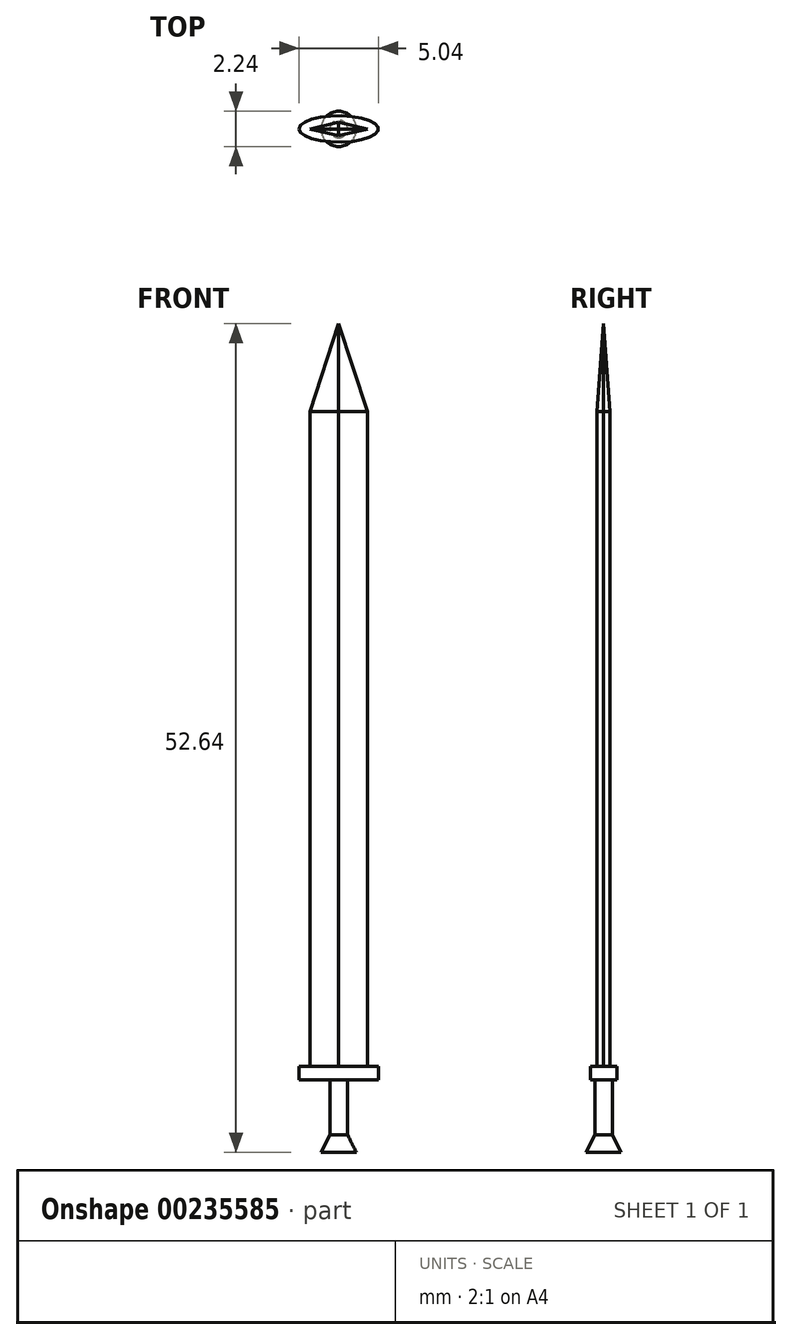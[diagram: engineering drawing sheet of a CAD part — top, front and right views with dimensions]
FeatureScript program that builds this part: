
annotation { "Feature Type Name" : "Feature", "Feature Type Description" : "" }
export const myFeature = defineFeature(function(context is Context, id is Id, definition is map)
    precondition{}
    {
        {
            var Q0;
            Q0=qCreatedBy(makeId("Top.planeOp"),FACE);
            var sketch = newSketch(context, id + "F0", { "sketchPlane" : qUnion([Q0])});
            skCircle(sketch, "E0", {"center": v(12.97, 4.08) * mm, "radius": 0.8 * mm});
            skSolve(sketch);
        }
        {
            var Q0;
            Q0=qCreatedBy(makeId("Top.planeOp"),FACE);
            cPlane(context, id + "F1", {"entities" : qUnion([Q0]), "cplaneType" : CPlaneType.OFFSET, "offset" : 0.8 * mm, "width" : 150 * mm, "height" : 150 * mm});
        }
        {
            var Q0;
            Q0=qCreatedBy(id+"F1.planeOp",FACE);
            var sketch = newSketch(context, id + "F2", { "sketchPlane" : qUnion([Q0])});
            skCircle(sketch, "E1.0", {"center": v(12.97, 4.08) * mm, "radius": 0.8 * mm, "construction": true});
            skCircle(sketch, "E2", {"center": v(12.97, 4.08) * mm, "radius": 0.4 * mm});
            skSolve(sketch);
        }
        {
            var Q0;
            Q0=qCreatedBy(id+"F1.planeOp",FACE);
            cPlane(context, id + "F3", {"entities" : qUnion([Q0]), "cplaneType" : CPlaneType.OFFSET, "offset" : 2.8 * mm, "width" : 150 * mm, "height" : 150 * mm});
        }
        {
            var Q0;
            Q0=qCreatedBy(id+"F3.planeOp",FACE);
            var sketch = newSketch(context, id + "F4", { "sketchPlane" : qUnion([Q0])});
            skCircle(sketch, "E3.0", {"center": v(12.97, 4.08) * mm, "radius": 0.4 * mm, "construction": true});
            skEllipse(sketch, "E4", {"center": v(12.97, 4.08) * mm, "majorRadius": 1.8 * mm, "minorRadius": 0.6 * mm, "majorAxis": v(-1, 0)});
            skSolve(sketch);
        }
        {
            var Q0;
            Q0=makeQuery(id+"F0.imprint","IMPRINT",FACE,{"disambiguationData":[TD([[makeQuery(id+"F0.imprint","IMPRINT",EDGE,{"derivedFrom":sQuery(id+"F0.wireOp",EDGE,"E0")}),1.0]])]});
            var Q1;
            Q1=makeQuery(id+"F2.imprint","IMPRINT",FACE,{"disambiguationData":[TD([[makeQuery(id+"F2.imprint","IMPRINT",EDGE,{"derivedFrom":sQuery(id+"F2.wireOp",EDGE,"E2")}),1.0]])]});
            loft(context, id + "F5", {"sheetProfilesArray" : [{ "sheetProfileEntities" : qUnion([Q0]) }, { "sheetProfileEntities" : qUnion([Q1]) }]});
        }
        {
            var Q0;
            Q0=makeQuery(id+"F5.opLoft","CAP_FACE",FACE,{"disambiguationData":[OSD([makeQuery(id+"F2.imprint","IMPRINT",FACE,{"disambiguationData":[TD([[makeQuery(id+"F2.imprint","IMPRINT",EDGE,{"derivedFrom":sQuery(id+"F2.wireOp",EDGE,"E2")}),1.0]])]})])],"isStart":true});
            extrude(context, id + "F6", {"entities" : qUnion([Q0]), "operationType" : NewBodyOperationType.ADD, "depth" : 2.6 * mm});
        }
        {
            var Q0;
            Q0=makeQuery(id+"F4.imprint","IMPRINT",FACE,{"disambiguationData":[TD([[makeQuery(id+"F4.imprint","IMPRINT",EDGE,{"derivedFrom":sQuery(id+"F4.wireOp",EDGE,"E4")}),1.0]])]});
            extrude(context, id + "F7", {"entities" : qUnion([Q0]), "operationType" : NewBodyOperationType.ADD, "endBound" : BoundingType.SYMMETRIC, "depth" : 0.6 * mm});
        }
        {
            var Q0;
            Q0=qCreatedBy(id+"F3.planeOp",FACE);
            cPlane(context, id + "F8", {"entities" : qUnion([Q0]), "cplaneType" : CPlaneType.OFFSET, "offset" : 0 * mm, "width" : 150 * mm, "height" : 150 * mm});
        }
        {
            var Q0;
            Q0=qCreatedBy(id+"F8.planeOp",FACE);
            var sketch = newSketch(context, id + "F9", { "sketchPlane" : qUnion([Q0])});
            skEllipse(sketch, "E5.0", {"center": v(12.97, 4.08) * mm, "majorRadius": 1.8 * mm, "minorRadius": 0.6 * mm, "majorAxis": v(-1, 0), "construction": true});
            skLineSegment(sketch, "E6", {"start": v(12.97, 5.3) * mm, "end": v(12.97, 2.6) * mm, "construction": true});
            skPoint(sketch, "E6.endSnap0", {"position": v(12.97, 3.48) * mm});
            skLineSegment(sketch, "E7", {"start": v(10.7, 4.08) * mm, "end": v(15.43, 4.08) * mm, "construction": true});
            skPoint(sketch, "E7.startSnap0", {"position": v(11.17, 4.08) * mm});
            skLineSegment(sketch, "E8", {"start": v(11.67, 4.08) * mm, "end": v(12.97, 4.38) * mm});
            skLineSegment(sketch, "E9", {"start": v(12.97, 4.38) * mm, "end": v(14.27, 4.08) * mm});
            skLineSegment(sketch, "E10", {"start": v(14.27, 4.08) * mm, "end": v(12.97, 3.78) * mm});
            skLineSegment(sketch, "E11", {"start": v(12.97, 3.78) * mm, "end": v(11.67, 4.08) * mm});
            skSolve(sketch);
        }
        {
            var Q0;
            Q0 = qSketchRegion(id + "F9", true);
            extrude(context, id + "F10", {"entities" : qUnion([Q0]), "operationType" : NewBodyOperationType.ADD, "depth" : 30 * mm});
        }
        {
            var Q0;
            Q0=makeQuery(id+"F10.opExtrude","CAP_FACE",FACE,{"disambiguationData":[OSD([sQuery(id+"F9.wireOp",EDGE,"E8"),sQuery(id+"F9.wireOp",EDGE,"E9"),sQuery(id+"F9.wireOp",EDGE,"E10"),sQuery(id+"F9.wireOp",EDGE,"E11")])],"isStart":false});
            cPlane(context, id + "F11", {"entities" : qUnion([Q0]), "cplaneType" : CPlaneType.OFFSET, "offset" : 4 * mm, "width" : 150 * mm, "height" : 150 * mm});
        }
        {
            var Q0;
            Q0=qCreatedBy(id+"F11.planeOp",FACE);
            var sketch = newSketch(context, id + "F12", { "sketchPlane" : qUnion([Q0])});
            skLineSegment(sketch, "E12.0", {"start": v(12.97, 4.38) * mm, "end": v(14.27, 4.08) * mm, "construction": true});
            skLineSegment(sketch, "E13.0", {"start": v(11.67, 4.08) * mm, "end": v(12.97, 4.38) * mm, "construction": true});
            skLineSegment(sketch, "E14.0", {"start": v(12.97, 3.78) * mm, "end": v(11.67, 4.08) * mm, "construction": true});
            skLineSegment(sketch, "E15.0", {"start": v(14.27, 4.08) * mm, "end": v(12.97, 3.78) * mm, "construction": true});
            skPoint(sketch, "E16", {"position": v(12.97, 4.08) * mm});
            skCircle(sketch, "E17", {"center": v(12.97, 4.08) * mm, "radius": 0 * mm});
            skSolve(sketch);
        }
        {
            var Q1;
            Q1=makeQuery(id+"F10.opExtrude","CAP_FACE",FACE,{"disambiguationData":[OSD([sQuery(id+"F9.wireOp",EDGE,"E8"),sQuery(id+"F9.wireOp",EDGE,"E9"),sQuery(id+"F9.wireOp",EDGE,"E10"),sQuery(id+"F9.wireOp",EDGE,"E11")])],"isStart":false});
            var Q2;
            Q2=sQuery(id+"F12.wireOp",VERTEX,"E16");
            loft(context, id + "F13", {"operationType" : NewBodyOperationType.ADD, "sheetProfilesArray" : [{ "sheetProfileEntities" : qUnion([Q1]) }, { "sheetProfileEntities" : qUnion([Q2]) }]});
        }
        {
            var Q0;
            Q0=makeQuery(id+"F5.opLoft","SWEPT_BODY",BODY,{"disambiguationData":[OSD([makeQuery(id+"F0.imprint","IMPRINT",FACE,{"disambiguationData":[TD([[makeQuery(id+"F0.imprint","IMPRINT",EDGE,{"derivedFrom":sQuery(id+"F0.wireOp",EDGE,"E0")}),1.0]])]}),makeQuery(id+"F2.imprint","IMPRINT",FACE,{"disambiguationData":[TD([[makeQuery(id+"F2.imprint","IMPRINT",EDGE,{"derivedFrom":sQuery(id+"F2.wireOp",EDGE,"E2")}),1.0]])]})])]});
            var Q1;
            Q1=qCreatedBy(makeId("Origin.pointOp"),VERTEX);
            transform(context, id + "F14", {"entities" : qUnion([Q0]), "transformType" : TransformType.SCALE_UNIFORMLY, "scale" : 1.4, "scalePoint" : qUnion([Q1]), "makeCopy" : false});
        }
    });
